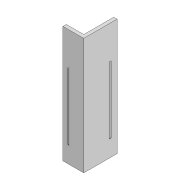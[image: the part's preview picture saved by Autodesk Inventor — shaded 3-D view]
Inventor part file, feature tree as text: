
AUTODESK INVENTOR PART (.ipt)
format: ipt  version: 2022 (Build 260153000, 153)  size: 130,560 bytes
history: native  units: mm
features: projected_geometry x6, extrude x3, sketch x3
ambient origin geometry x8: Origin, YZ Plane, XZ Plane, XY Plane, X Axis, Y Axis, Z Axis, Center Point
bodies: Solid1 (feature_tree)
feature tree (12):
  extrude  "Extrusion1"  Depth=4.0mm
  extrude  "Extrusion2"  Depth=25.0mm
  extrude  "Extrusion3"  TaperAngle=30.0deg  [1 undecoded]
  sketch  "Sketch1"  dims[d0=4.0mm d1=4.0mm]
  sketch  "Sketch2"  dims[d2=40.0mm d3=25.0mm]
  projected_geometry  "Projected Loop1"
  sketch  "Sketch3"  dims[d4=100.0mm d5=0.0mm d7=30.0deg d8=1.0mm d9=80.0mm d10=0.0mm d11=20.0mm d12=40.0mm d13=0.0mm]
  projected_geometry  "Projected Loop2"
  projected_geometry  "Projected Loop3"
  projected_geometry  "Projected Loop4"
  projected_geometry  "Projected Loop5"
  projected_geometry  "Projected Loop6"
note: 1 required parameter value undecoded (feature->parameter linkage not recoverable at this tier; creation-order binding heuristic only, values carry confidence <= 0.55)
